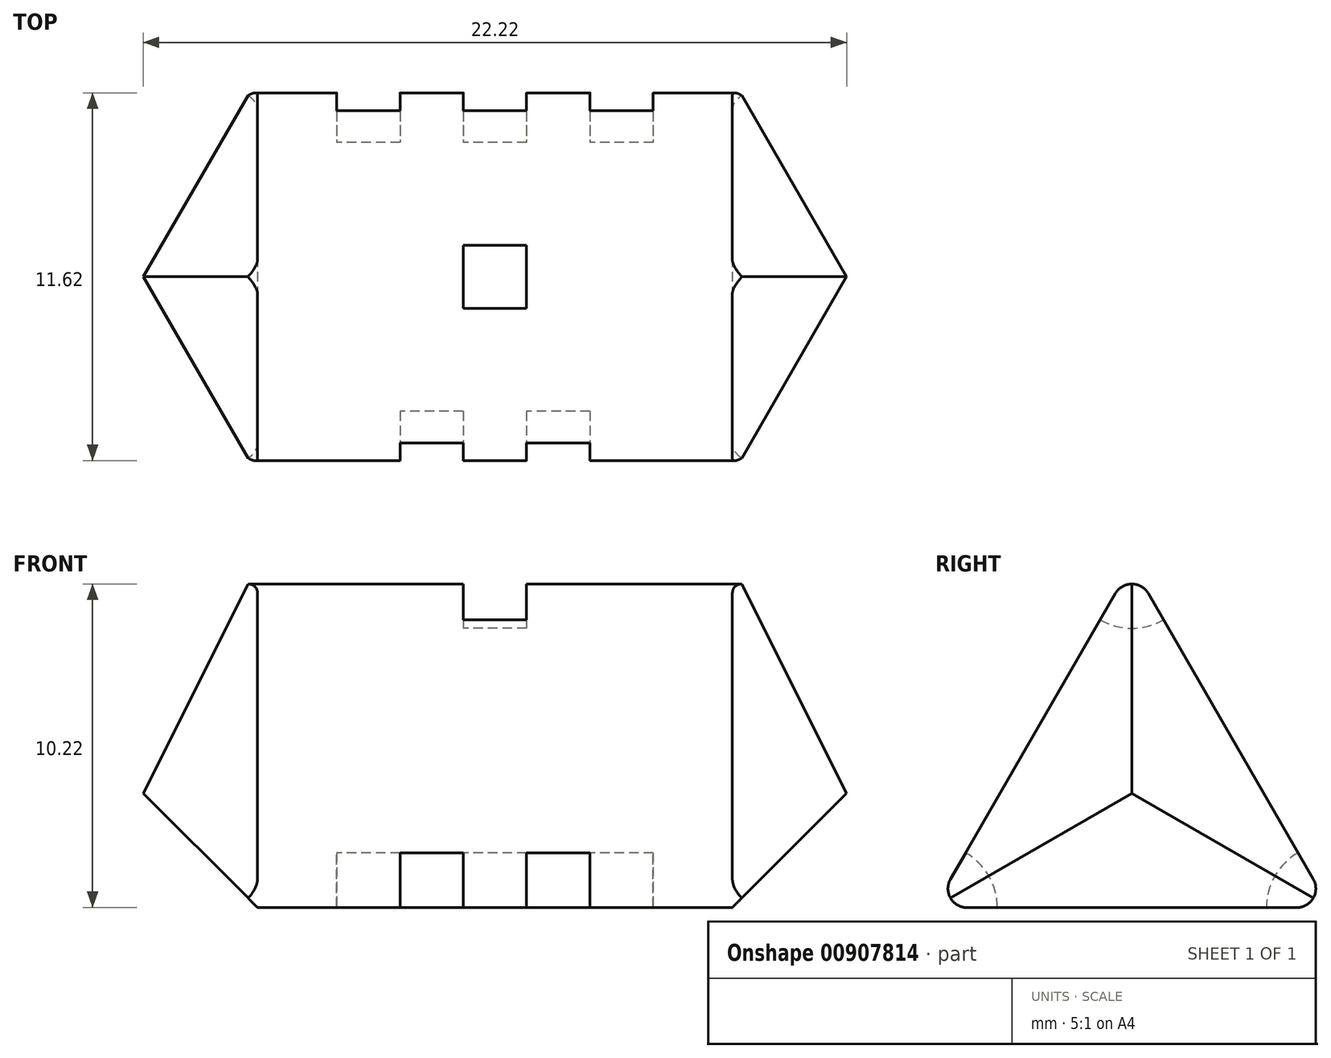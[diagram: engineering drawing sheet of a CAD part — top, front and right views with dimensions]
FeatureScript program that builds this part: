
annotation { "Feature Type Name" : "Feature", "Feature Type Description" : "" }
export const myFeature = defineFeature(function(context is Context, id is Id, definition is map)
    precondition{}
    {
        {
            var Q0;
            Q0=qCreatedBy(makeId("Right.planeOp"),FACE);
            var sketch = newSketch(context, id + "F0", { "sketchPlane" : qUnion([Q0])});
            skLineSegment(sketch, "E0", {"start": v(6.25, 2.17) * mm, "end": v(0, 13) * mm});
            skLineSegment(sketch, "E1", {"start": v(0, 13) * mm, "end": v(-6.25, 2.17) * mm});
            skLineSegment(sketch, "E2", {"start": v(6.25, 2.17) * mm, "end": v(-6.25, 2.17) * mm});
            skArc(sketch, "E3", {"start": v(5.25, 3.9) * mm, "mid": v(4.52, 3.17) * mm, "end": v(4.25, 2.17) * mm});
            skArc(sketch, "E4", {"start": v(-4.25, 2.17) * mm, "mid": v(-4.52, 3.17) * mm, "end": v(-5.25, 3.9) * mm});
            skArc(sketch, "E5", {"start": v(-1, 11.26) * mm, "mid": v(0, 11) * mm, "end": v(1, 11.26) * mm});
            skSolve(sketch);
        }
        {
            var Q0;
            Q0=makeQuery(id+"F0.imprint","IMPRINT",FACE,{"disambiguationData":[TD([[makeQuery(id+"F0.imprint","IMPRINT",EDGE,{"derivedFrom":sQuery(id+"F0.wireOp",EDGE,"E0")}),1.0]])]});
            var Q1;
            {var subQ0=sQuery(id+"F0.wireOp",EDGE,"BqEqU8mU-FlL4-bfzw-Q86g-FavSRKaAhhkT");var subQ5=sQuery(id+"F0.wireOp",EDGE,"E0");var subQ6=makeQuery(id+"F0.imprint","INTERSECT",VERTEX,{"derivedFrom":[subQ5,subQ0]});Q1=makeQuery(id+"F0.imprint","IMPRINT",FACE,{"disambiguationData":[TD([[makeQuery(id+"F0.imprint","IMPRINT",EDGE,{"disambiguationData":[TD([[subQ6,-1.0]])],"derivedFrom":subQ5}),1.0]])]});}
            var Q2;
            {var subQ0=sQuery(id+"F0.wireOp",EDGE,"E2");var subQ1=sQuery(id+"F0.wireOp",EDGE,"E1");var subQ2=makeQuery(id+"F0.imprint","INTERSECT",VERTEX,{"derivedFrom":[subQ1,subQ0]});Q2=makeQuery(id+"F0.imprint","IMPRINT",FACE,{"disambiguationData":[TD([[makeQuery(id+"F0.imprint","IMPRINT",EDGE,{"disambiguationData":[TD([[subQ2,1.0]])],"derivedFrom":subQ1}),1.0]])]});}
            var Q3;
            {var subQ0=sQuery(id+"F0.wireOp",EDGE,"E3");Q3=makeQuery(id+"F0.imprint","IMPRINT",FACE,{"disambiguationData":[TD([[makeQuery(id+"F0.imprint","IMPRINT",EDGE,{"derivedFrom":subQ0}),-1.0]])]});}
            extrude(context, id + "F1", {"entities" : qUnion([Q0, Q1, Q2, Q3]), "depth" : 15 * mm, "offsetDistance" : 25 * mm});
        }
        {
            var Q0;
            Q0=makeQuery(id+"F1.opExtrude","CAP_FACE",FACE,{"disambiguationData":[OSD([sQuery(id+"F0.wireOp",EDGE,"E0"),sQuery(id+"F0.wireOp",EDGE,"E1"),sQuery(id+"F0.wireOp",EDGE,"E2")])],"isStart":true});
            extrude(context, id + "F2", {"entities" : qUnion([Q0]), "operationType" : NewBodyOperationType.ADD, "depth" : 25 * mm, "offsetDistance" : 25 * mm, "hasDraft" : true, "draftAngle" : 45 * degree, "draftPullDirection" : true});
        }
        {
            var Q0;
            Q0=makeQuery(id+"F1.opExtrude","CAP_FACE",FACE,{"disambiguationData":[OSD([sQuery(id+"F0.wireOp",EDGE,"E0"),sQuery(id+"F0.wireOp",EDGE,"E1"),sQuery(id+"F0.wireOp",EDGE,"E2")])],"isStart":false});
            extrude(context, id + "F3", {"entities" : qUnion([Q0]), "operationType" : NewBodyOperationType.ADD, "depth" : 25 * mm, "offsetDistance" : 25 * mm, "hasDraft" : true, "draftAngle" : 45 * degree, "draftPullDirection" : true});
        }
        {
            var Q0;
            Q0=makeQuery(id+"F1.opExtrude","SWEPT_EDGE",EDGE,{"disambiguationData":[OSD([sQuery(id+"F0.wireOp",EDGE,"E0"),sQuery(id+"F0.wireOp",EDGE,"E1")])]});
            var Q1;
            Q1=makeQuery(id+"F1.opExtrude","SWEPT_EDGE",EDGE,{"disambiguationData":[OSD([sQuery(id+"F0.wireOp",EDGE,"E1"),sQuery(id+"F0.wireOp",EDGE,"E2")])]});
            var Q2;
            Q2=makeQuery(id+"F1.opExtrude","SWEPT_EDGE",EDGE,{"disambiguationData":[OSD([sQuery(id+"F0.wireOp",EDGE,"E0"),sQuery(id+"F0.wireOp",EDGE,"E2")])]});
            fillet(context, id + "F4", {"entities" : qUnion([Q0, Q1, Q2]), "radius" : 0.6 * mm, "tangentPropagation" : true, "allowEdgeOverflow" : false});
        }
        {
            var Q0;
            {var subQ3=sQuery(id+"F0.wireOp",EDGE,"E5");Q0=makeQuery(id+"F0.imprint","IMPRINT",FACE,{"disambiguationData":[TD([[makeQuery(id+"F0.imprint","IMPRINT",EDGE,{"derivedFrom":subQ3}),1.0]])]});}
            extrude(context, id + "F5", {"entities" : qUnion([Q0]), "operationType" : NewBodyOperationType.REMOVE, "depth" : 8.5 * mm, "offsetDistance" : 25 * mm, "hasSecondDirection" : true, "secondDirectionOppositeDirection" : false, "secondDirectionDepth" : 6.5 * mm});
        }
        {
            var Q0;
            {var subQ3=sQuery(id+"F0.wireOp",EDGE,"E4");Q0=makeQuery(id+"F0.imprint","IMPRINT",FACE,{"disambiguationData":[TD([[makeQuery(id+"F0.imprint","IMPRINT",EDGE,{"derivedFrom":subQ3}),1.0]])]});}
            extrude(context, id + "F6", {"entities" : qUnion([Q0]), "operationType" : NewBodyOperationType.REMOVE, "depth" : 6.5 * mm, "offsetDistance" : 25 * mm, "hasSecondDirection" : true, "secondDirectionOppositeDirection" : false, "secondDirectionDepth" : 4.5 * mm});
        }
        {
            var Q0;
            {var subQ3=sQuery(id+"F0.wireOp",EDGE,"E4");Q0=makeQuery(id+"F0.imprint","IMPRINT",FACE,{"disambiguationData":[TD([[makeQuery(id+"F0.imprint","IMPRINT",EDGE,{"derivedFrom":subQ3}),1.0]])]});}
            extrude(context, id + "F7", {"entities" : qUnion([Q0]), "operationType" : NewBodyOperationType.REMOVE, "depth" : 10.5 * mm, "offsetDistance" : 25 * mm, "hasSecondDirection" : true, "secondDirectionOppositeDirection" : false, "secondDirectionDepth" : 8.5 * mm});
        }
        {
            var Q0;
            {var subQ3=sQuery(id+"F0.wireOp",EDGE,"E3");Q0=makeQuery(id+"F0.imprint","IMPRINT",FACE,{"disambiguationData":[TD([[makeQuery(id+"F0.imprint","IMPRINT",EDGE,{"derivedFrom":subQ3}),1.0]])]});}
            extrude(context, id + "F8", {"entities" : qUnion([Q0]), "operationType" : NewBodyOperationType.REMOVE, "depth" : 4.5 * mm, "offsetDistance" : 25 * mm, "hasSecondDirection" : true, "secondDirectionOppositeDirection" : false, "secondDirectionDepth" : 2.5 * mm});
        }
        {
            var Q0;
            {var subQ3=sQuery(id+"F0.wireOp",EDGE,"E3");Q0=makeQuery(id+"F0.imprint","IMPRINT",FACE,{"disambiguationData":[TD([[makeQuery(id+"F0.imprint","IMPRINT",EDGE,{"derivedFrom":subQ3}),1.0]])]});}
            extrude(context, id + "F9", {"entities" : qUnion([Q0]), "operationType" : NewBodyOperationType.REMOVE, "depth" : 8.5 * mm, "offsetDistance" : 25 * mm, "hasSecondDirection" : true, "secondDirectionOppositeDirection" : false, "secondDirectionDepth" : 6.5 * mm});
        }
        {
            var Q0;
            {var subQ3=sQuery(id+"F0.wireOp",EDGE,"E3");Q0=makeQuery(id+"F0.imprint","IMPRINT",FACE,{"disambiguationData":[TD([[makeQuery(id+"F0.imprint","IMPRINT",EDGE,{"derivedFrom":subQ3}),1.0]])]});}
            extrude(context, id + "F10", {"entities" : qUnion([Q0]), "operationType" : NewBodyOperationType.REMOVE, "depth" : 12.5 * mm, "offsetDistance" : 25 * mm, "hasSecondDirection" : true, "secondDirectionOppositeDirection" : false, "secondDirectionDepth" : 10.5 * mm});
        }
    });
